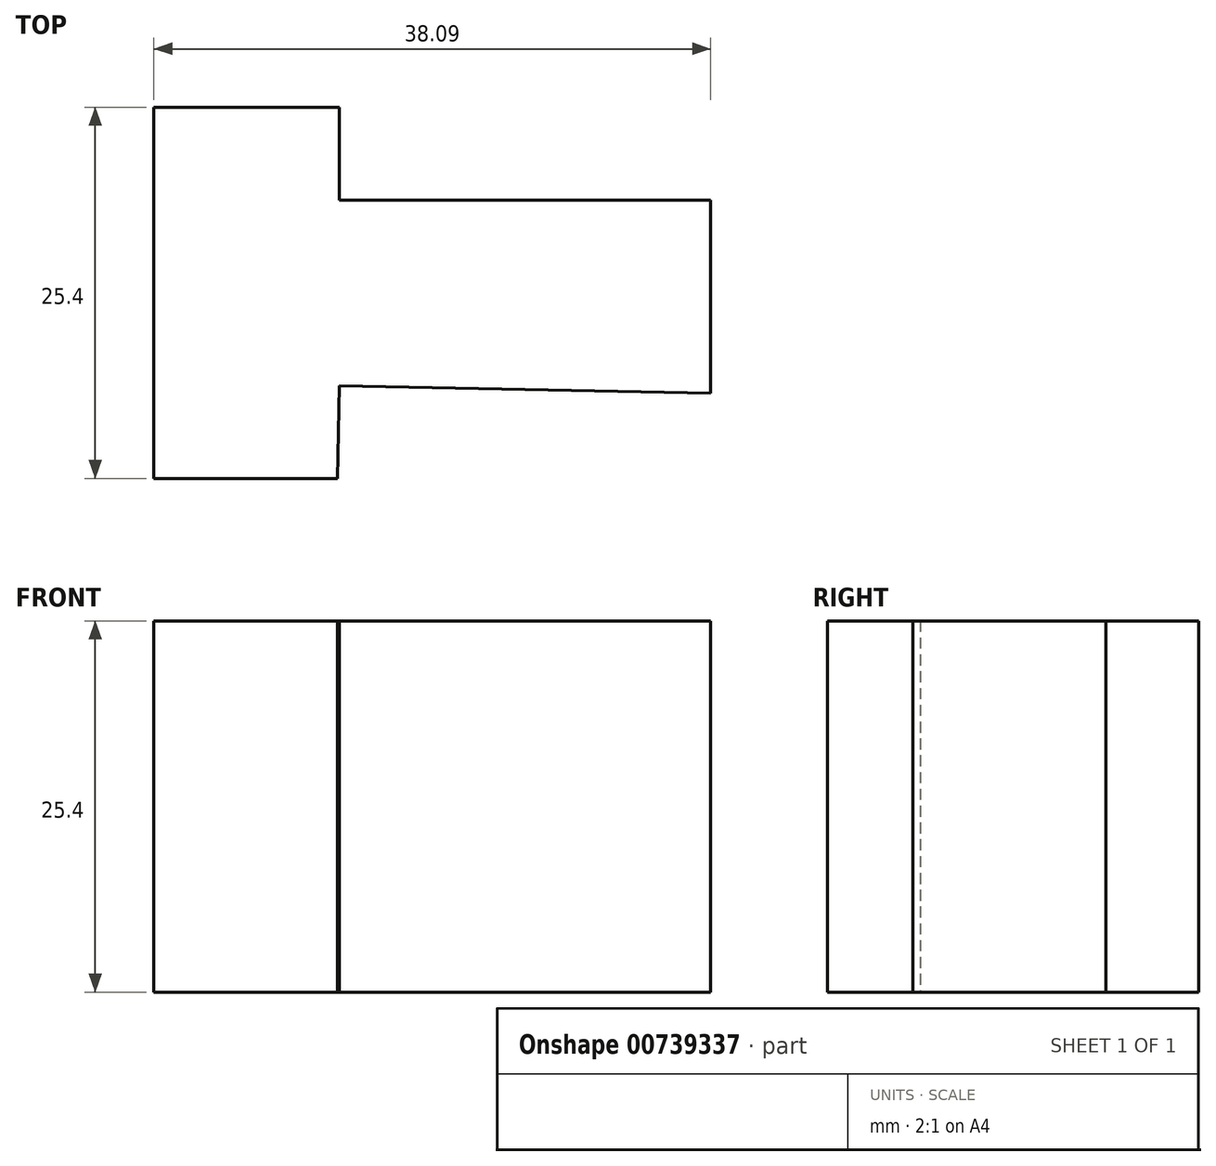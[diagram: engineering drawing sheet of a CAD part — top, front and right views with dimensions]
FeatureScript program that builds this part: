
annotation { "Feature Type Name" : "Feature", "Feature Type Description" : "" }
export const myFeature = defineFeature(function(context is Context, id is Id, definition is map)
    precondition{}
    {
        {
            var Q0;
            Q0=qCreatedBy(makeId("Top.planeOp"),FACE);
            var sketch = newSketch(context, id + "F0", { "sketchPlane" : qUnion([Q0])});
            skLineSegment(sketch, "E0", {"start": v(0, 0) * mm, "end": v(0, 25.4) * mm});
            skLineSegment(sketch, "E1", {"start": v(0, 25.4) * mm, "end": v(12.7, 25.4) * mm});
            skLineSegment(sketch, "E2", {"start": v(12.7, 25.4) * mm, "end": v(12.7, 19.05) * mm});
            skLineSegment(sketch, "E3", {"start": v(0, 0) * mm, "end": v(12.57, 0) * mm});
            skLineSegment(sketch, "E4", {"start": v(12.57, 0) * mm, "end": v(12.7, 6.35) * mm});
            skLineSegment(sketch, "E5", {"start": v(12.7, 6.35) * mm, "end": v(38.1, 5.83) * mm});
            skLineSegment(sketch, "E6", {"start": v(38.1, 5.83) * mm, "end": v(38.1, 19.05) * mm});
            skLineSegment(sketch, "E7", {"start": v(38.1, 19.05) * mm, "end": v(12.7, 19.05) * mm});
            skSolve(sketch);
        }
        {
            var Q0;
            Q0 = qSketchRegion(id + "F0", true);
            extrude(context, id + "F1", {"entities" : qUnion([Q0]), "depth" : 25.4 * mm, "offsetDistance" : 25.4 * mm});
        }
    });
